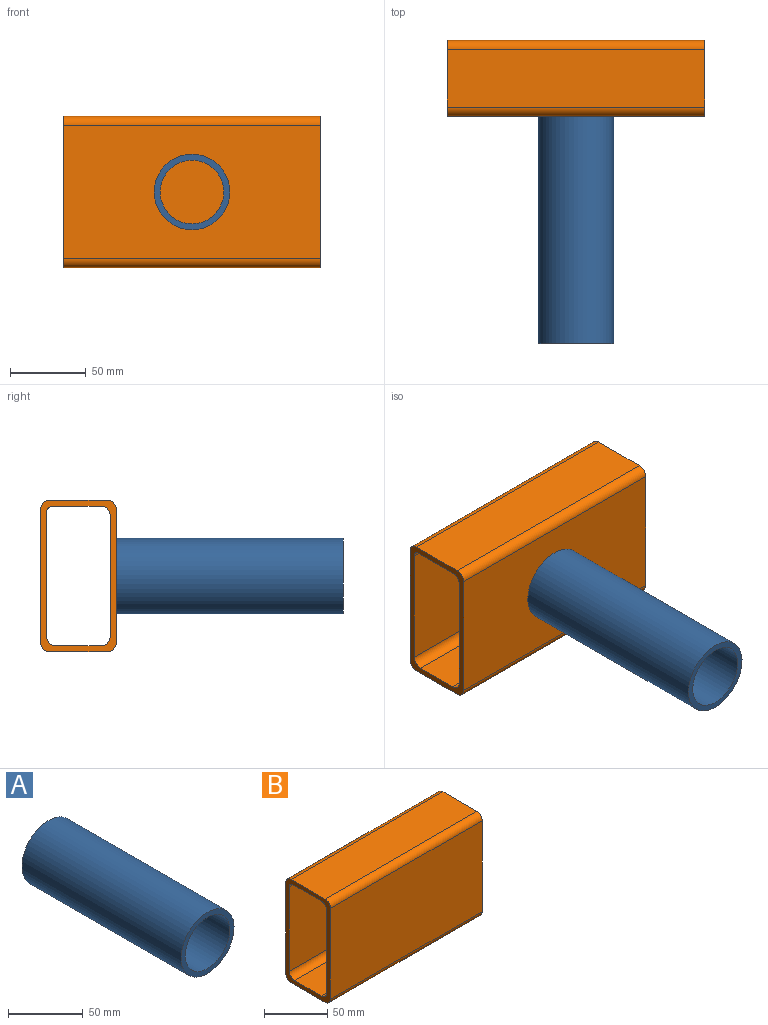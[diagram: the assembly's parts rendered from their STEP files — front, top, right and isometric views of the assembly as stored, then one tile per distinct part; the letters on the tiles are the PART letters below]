
ASSEMBLY  parts=2 mates=1
PART A: 4 faces, bbox 50x150x50 mm
  f0: cylinder r=21mm len=150mm, axis (0,1,0), area 19792mm2, adj f2,f3
  f1: cylinder r=25mm len=150mm, axis (0,1,0), area 23561.9mm2, adj f2,f3
  f2: plane 50x50mm, normal (0,-1,0), area 578.1mm2, adj f0,f1
  f3: plane 50x50mm, normal (0,1,0), area 578.1mm2, adj f0,f1
PART B: 18 faces, bbox 170x50x100 mm
  f0: plane 170x38mm, normal (0,0,1), area 6460mm2, adj f1,f15,f16,f17
  f1: cylinder r=6mm len=170mm, axis (-1,0,0), area 1602.2mm2, adj f0,f2,f16,f17
  f2: plane 170x88mm, normal (0,-1,0), area 14960mm2, adj f1,f3,f16,f17
  f3: cylinder r=6mm len=170mm, axis (-1,0,0), area 1602.2mm2, adj f2,f4,f16,f17
  f4: plane 170x38mm, normal (0,0,-1), area 6460mm2, adj f3,f5,f16,f17
  f5: cylinder r=6mm len=170mm, axis (-1,0,0), area 1602.2mm2, adj f4,f6,f16,f17
  f6: plane 170x88mm, normal (0,1,0), area 14960mm2, adj f5,f15,f16,f17
  f7: cylinder r=6mm len=170mm, axis (-1,0,0), area 1602.2mm2, adj f8,f14,f16,f17
  f8: plane 170x30mm, normal (0,0,1), area 5100mm2, adj f7,f9,f16,f17
  f9: cylinder r=6mm len=170mm, axis (-1,0,0), area 1602.2mm2, adj f8,f10,f16,f17
  f10: plane 170x80mm, normal (0,1,0), area 13600mm2, adj f9,f11,f16,f17
  f11: cylinder r=6mm len=170mm, axis (-1,0,0), area 1602.2mm2, adj f10,f12,f16,f17
  f12: plane 170x32mm, normal (0,0,-1), area 5440mm2, adj f11,f13,f16,f17
  f13: cylinder r=4mm len=170mm, axis (-1,0,0), area 1068.1mm2, adj f12,f14,f16,f17
  f14: plane 170x82mm, normal (0,-1,0), area 13940mm2, adj f7,f13,f16,f17
  f15: cylinder r=6mm len=170mm, axis (-1,0,0), area 1602.2mm2, adj f0,f6,f16,f17
  f16: plane 100x50mm, normal (1,0,0), area 1131.7mm2, adj f0,f1,f2,f3,f4,f5,f6,f7
  f17: plane 100x50mm, normal (-1,0,0), area 1131.7mm2, adj f0,f1,f2,f3,f4,f5,f6,f7
PLACE A t=(-13.48,40.88,-39.51)mm
PLACE B t=(-98.48,65.95,-39.44)mm fixed
MATE fastened B.f2 <-> A.f1  axis (0,-1,0) through (-13.48,40.88,-39.51)mm
